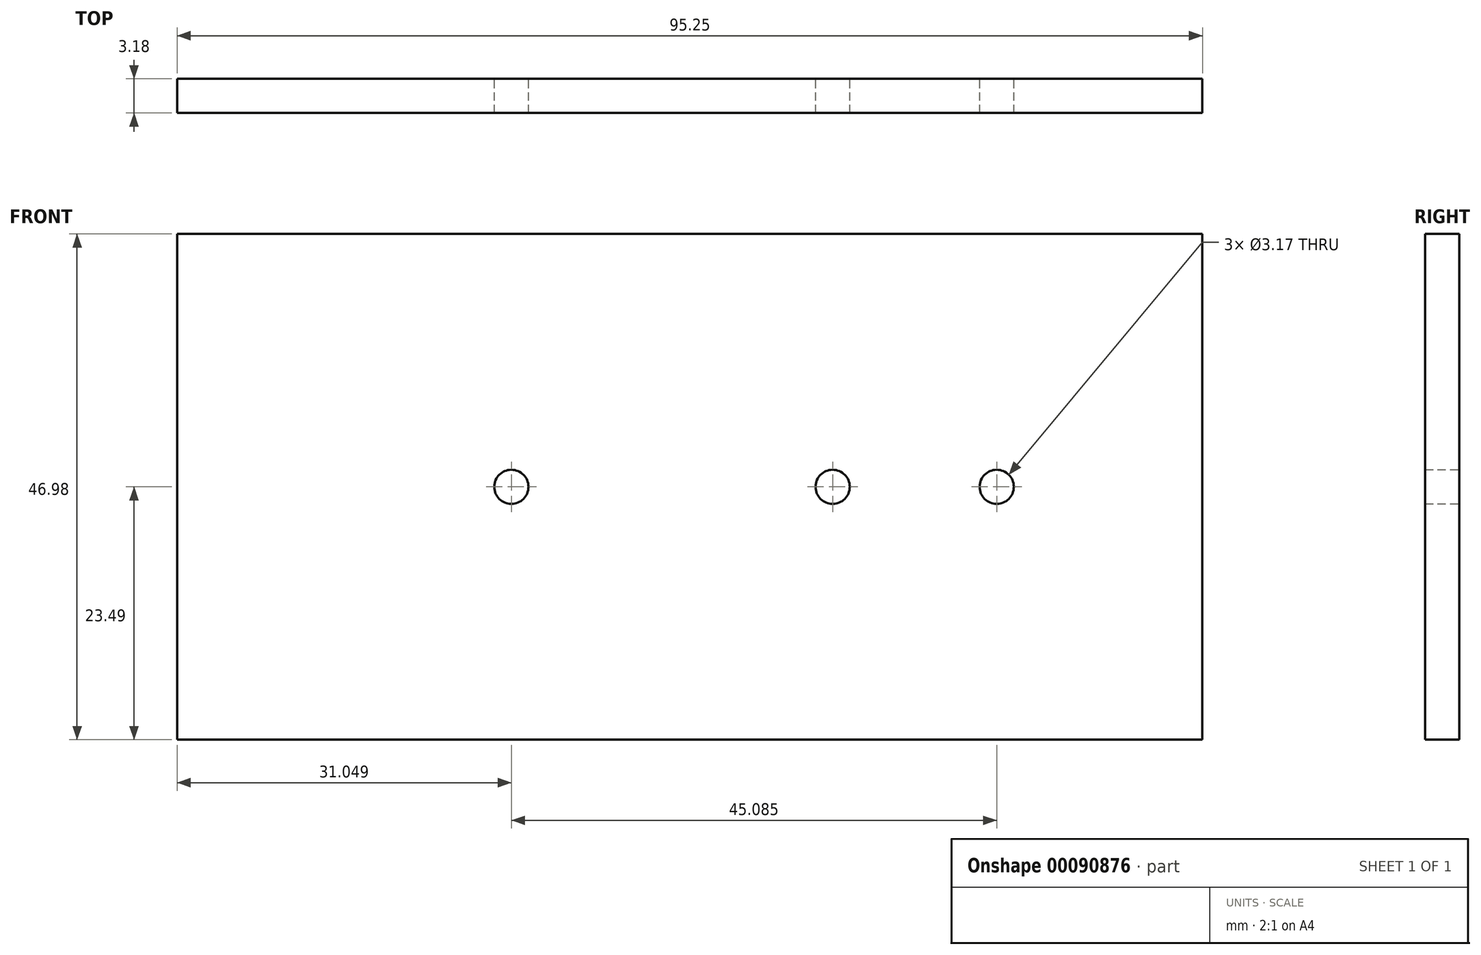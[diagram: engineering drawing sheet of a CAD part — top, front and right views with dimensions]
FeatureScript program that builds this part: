
annotation { "Feature Type Name" : "Feature", "Feature Type Description" : "" }
export const myFeature = defineFeature(function(context is Context, id is Id, definition is map)
    precondition{}
    {
        {
            var Q0;
            Q0=qCreatedBy(makeId("Front.planeOp"),FACE);
            var sketch = newSketch(context, id + "F0", { "sketchPlane" : qUnion([Q0])});
            skLineSegment(sketch, "E0.bottom", {"start": v(-38.98, 23.5) * mm, "end": v(43.57, 23.5) * mm});
            skLineSegment(sketch, "E0.top", {"start": v(-38.98, -23.5) * mm, "end": v(43.57, -23.5) * mm});
            skLineSegment(sketch, "E0.right", {"start": v(43.57, 23.5) * mm, "end": v(43.57, -23.5) * mm});
            skCircle(sketch, "E1", {"center": v(-20.63, 0) * mm, "radius": 1.59 * mm});
            skCircle(sketch, "E2", {"center": v(9.21, 0) * mm, "radius": 1.59 * mm});
            skCircle(sketch, "E3", {"center": v(24.45, 0) * mm, "radius": 1.59 * mm});
            skLineSegment(sketch, "E4", {"start": v(-20.63, 0) * mm, "end": v(9.21, 0) * mm});
            skLineSegment(sketch, "E5", {"start": v(9.21, 0) * mm, "end": v(24.45, 0) * mm});
            skLineSegment(sketch, "E6", {"start": v(9.21, 0) * mm, "end": v(0.32, 0) * mm});
            skLineSegment(sketch, "E7", {"start": v(-20.63, 0) * mm, "end": v(0.32, 0) * mm});
            skLineSegment(sketch, "E8", {"start": v(9.21, 0) * mm, "end": v(18.1, 0) * mm});
            skLineSegment(sketch, "E9", {"start": v(18.1, 0) * mm, "end": v(24.45, 0) * mm});
            skLineSegment(sketch, "E10", {"start": v(43.57, 23.5) * mm, "end": v(-51.68, 23.5) * mm});
            skLineSegment(sketch, "E11", {"start": v(43.57, -23.5) * mm, "end": v(-51.68, -23.5) * mm});
            skLineSegment(sketch, "E12", {"start": v(-51.68, -23.5) * mm, "end": v(-51.68, 23.5) * mm});
            skSolve(sketch);
        }
        {
            var Q0;
            Q0 = qSketchRegion(id + "F0", true);
            extrude(context, id + "F1", {"entities" : qUnion([Q0]), "endBound" : BoundingType.SYMMETRIC, "depth" : 3.17 * mm});
        }
    });
